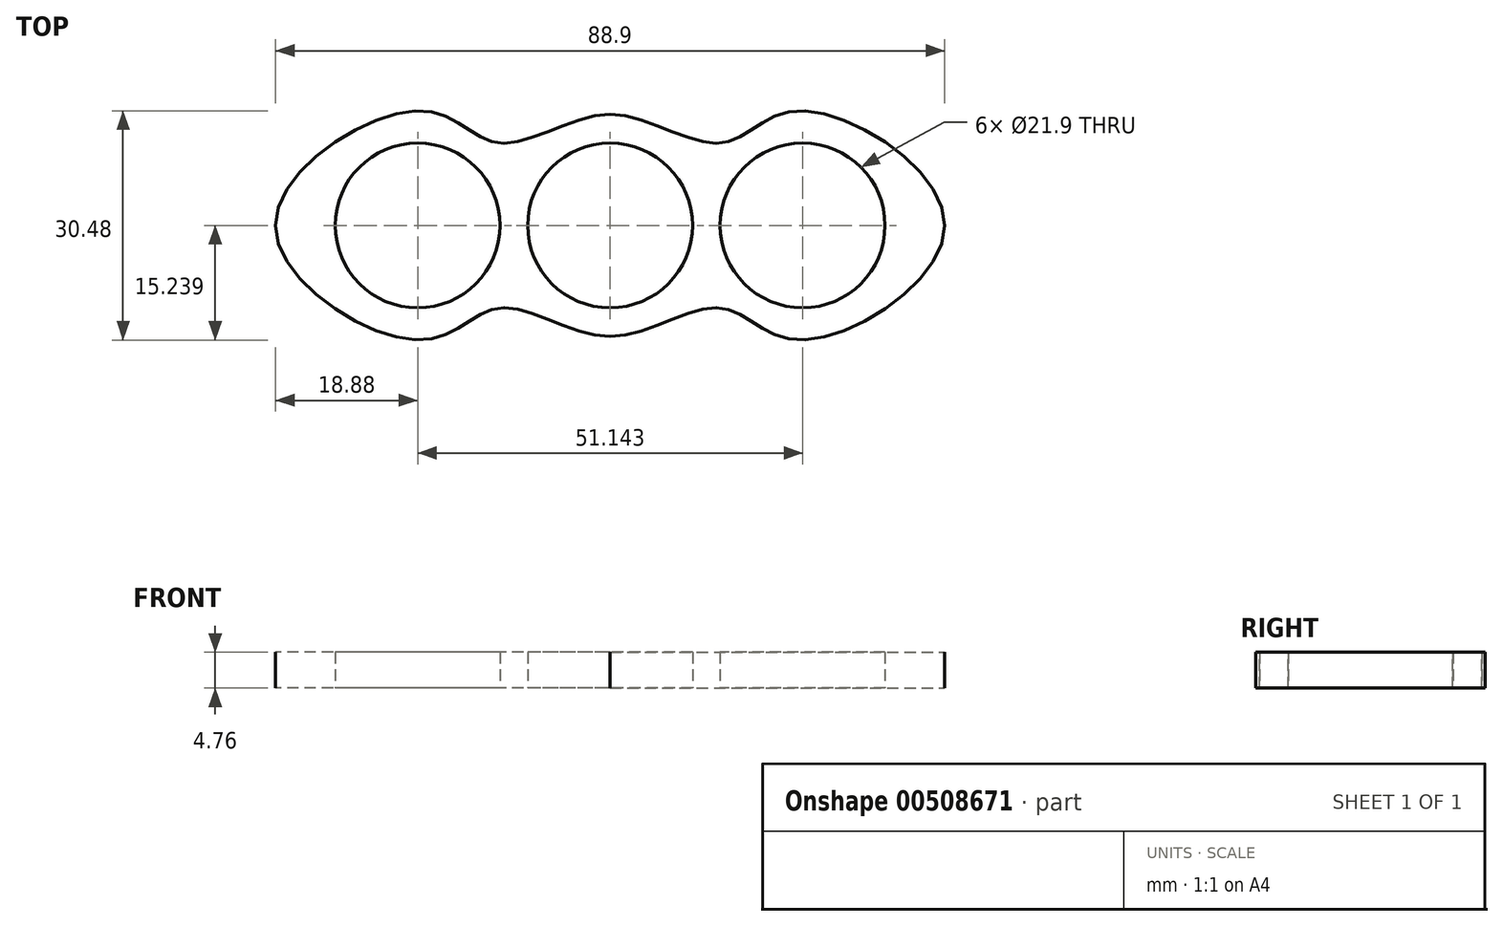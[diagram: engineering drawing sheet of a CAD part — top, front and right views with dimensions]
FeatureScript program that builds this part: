
annotation { "Feature Type Name" : "Feature", "Feature Type Description" : "" }
export const myFeature = defineFeature(function(context is Context, id is Id, definition is map)
    precondition{}
    {
        {
            var Q0;
            Q0=qCreatedBy(makeId("Top.planeOp"),FACE);
            var sketch = newSketch(context, id + "F0", { "sketchPlane" : qUnion([Q0])});
            skLineSegment(sketch, "E0.bottom", {"start": v(10.44, -3.53) * mm, "end": v(10.44, -3.53) * mm});
            skLineSegment(sketch, "E0.top", {"start": v(10.44, 26.95) * mm, "end": v(10.44, 26.95) * mm});
            skPoint(sketch, "E0.middle", {"position": v(-15.13, 11.7) * mm});
            skCircle(sketch, "E1", {"center": v(-15.13, 11.7) * mm, "radius": 10.95 * mm});
            skLineSegment(sketch, "E2", {"start": v(-15.13, 26.95) * mm, "end": v(-15.13, 22.66) * mm, "construction": true});
            skLineSegment(sketch, "E3", {"start": v(-15.13, 26.95) * mm, "end": v(-15.13, 26.95) * mm});
            skLineSegment(sketch, "E4", {"start": v(-40.7, -3.53) * mm, "end": v(-40.7, -3.53) * mm});
            skPoint(sketch, "E5", {"position": v(-15.13, 22.66) * mm});
            skLineSegment(sketch, "E6", {"start": v(-15.13, 22.66) * mm, "end": v(-44.44, 22.66) * mm, "construction": true});
            skLineSegment(sketch, "E7", {"start": v(-15.13, 11.7) * mm, "end": v(-15.13, -14.04) * mm, "construction": true});
            skLineSegment(sketch, "E8", {"start": v(-40.7, 26.95) * mm, "end": v(-40.7, 26.95) * mm});
            skPoint(sketch, "E9.orphan", {"position": v(-15.13, 47.2) * mm});
            skPoint(sketch, "E10", {"position": v(-29.78, 22.66) * mm});
            skFitSpline(sketch, "E11", {"points": [v(-15.13, 26.47) * mm, v(-29.78, 22.66) * mm, v(-40.25, 26.95) * mm, v(-59.58, 11.7) * mm], "startDerivative": vector(-45.32, 0.62) * mm, "endDerivative": vector(0.12, -55.35) * mm});
            skPoint(sketch, "E12.orphan", {"position": v(-63.58, 26.95) * mm});
            skFitSpline(sketch, "E13.MirrorCS", {"points": [v(-15.13, 26.47) * mm, v(-0.47, 22.66) * mm, v(10, 26.95) * mm, v(29.32, 11.7) * mm], "startDerivative": vector(45.32, 0.62) * mm, "endDerivative": vector(-0.12, -55.35) * mm});
            skFitSpline(sketch, "E14.MirrorCS", {"points": [v(-15.13, -3.05) * mm, v(-0.47, 0.76) * mm, v(10, -3.53) * mm, v(29.32, 11.7) * mm], "startDerivative": vector(45.32, -0.62) * mm, "endDerivative": vector(-0.12, 55.35) * mm});
            skFitSpline(sketch, "E15.MirrorCS", {"points": [v(-15.13, -3.05) * mm, v(-29.78, 0.76) * mm, v(-40.25, -3.53) * mm, v(-59.58, 11.7) * mm], "startDerivative": vector(-45.32, -0.62) * mm, "endDerivative": vector(0.12, 55.35) * mm});
            skPoint(sketch, "E16.orphan", {"position": v(25.32, 26.95) * mm});
            skPoint(sketch, "E17.orphan", {"position": v(3, -3.53) * mm});
            skPoint(sketch, "E18.orphan", {"position": v(-26.28, -3.53) * mm});
            skPoint(sketch, "E19.orphan", {"position": v(-55.58, -3.53) * mm});
            skLineSegment(sketch, "E20", {"start": v(-15.13, 26.95) * mm, "end": v(-79.91, 26.95) * mm, "construction": true});
            skCircle(sketch, "E21", {"center": v(-40.7, 11.7) * mm, "radius": 10.95 * mm});
            skCircle(sketch, "E22.MirrorC", {"center": v(10.44, 11.7) * mm, "radius": 10.95 * mm});
            skSolve(sketch);
        }
        {
            var Q0;
            Q0 = qSketchRegion(id + "F0", true);
            extrude(context, id + "F1", {"entities" : qUnion([Q0]), "depth" : 4.76 * mm});
        }
    });
